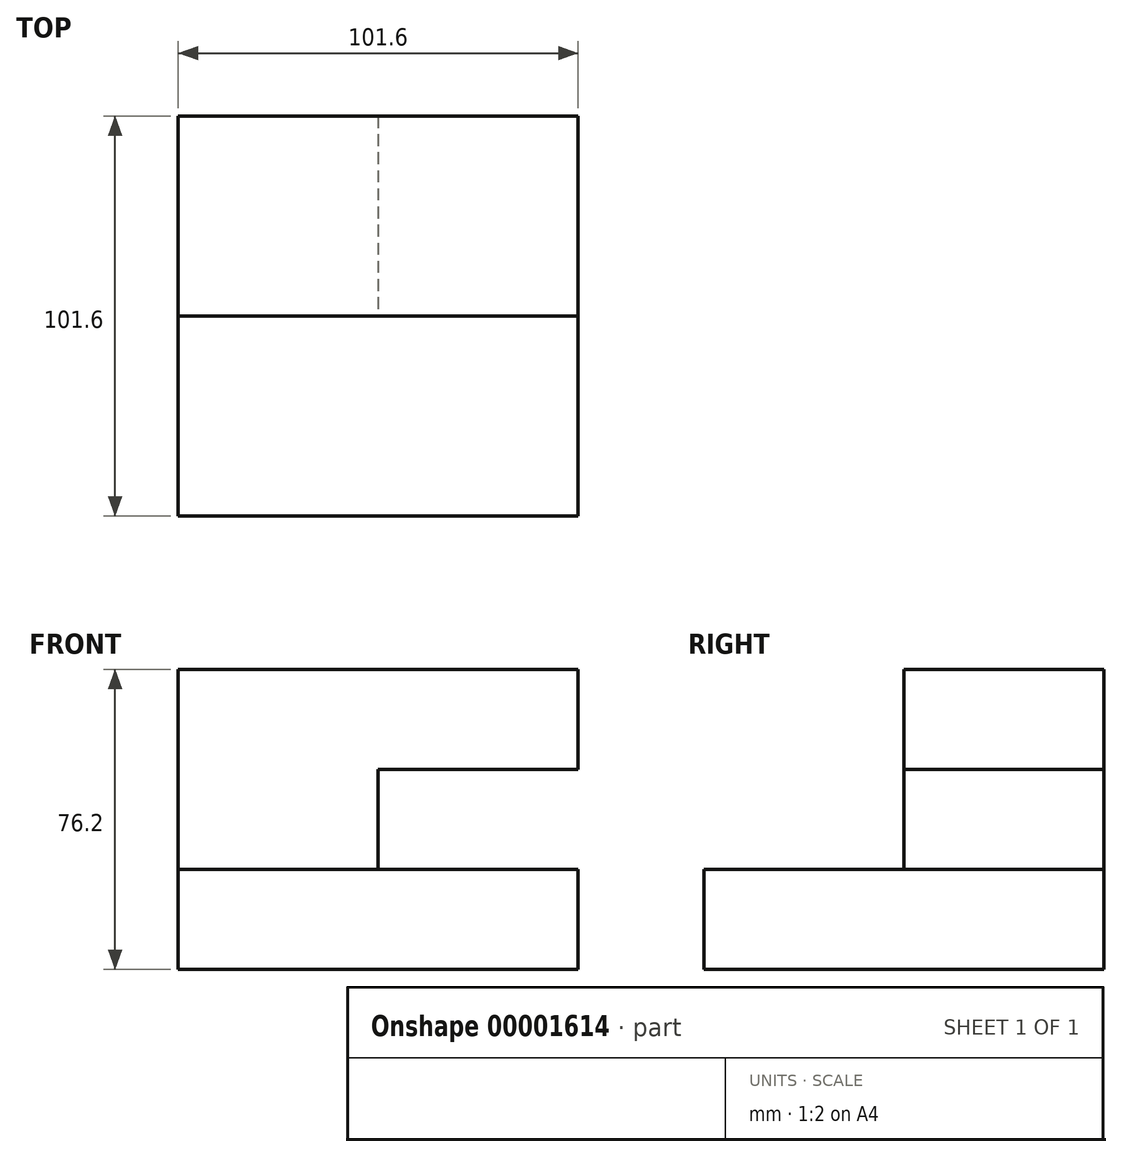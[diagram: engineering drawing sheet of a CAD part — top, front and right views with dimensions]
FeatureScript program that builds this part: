
annotation { "Feature Type Name" : "Feature", "Feature Type Description" : "" }
export const myFeature = defineFeature(function(context is Context, id is Id, definition is map)
    precondition{}
    {
        {
            var Q0;
            Q0=qCreatedBy(makeId("Top.planeOp"),FACE);
            var sketch = newSketch(context, id + "F0", { "sketchPlane" : qUnion([Q0])});
            skLineSegment(sketch, "E0.rect.bottom", {"start": v(50.8, 50.8) * mm, "end": v(-50.8, 50.8) * mm});
            skLineSegment(sketch, "E0.rect.top", {"start": v(50.8, -50.8) * mm, "end": v(-50.8, -50.8) * mm});
            skLineSegment(sketch, "E0.rect.left", {"start": v(50.8, 50.8) * mm, "end": v(50.8, -50.8) * mm});
            skLineSegment(sketch, "E0.rect.right", {"start": v(-50.8, 50.8) * mm, "end": v(-50.8, -50.8) * mm});
            skPoint(sketch, "E0.rect.middle", {"position": v(0, 0) * mm});
            skSolve(sketch);
        }
        {
            var Q0;
            Q0=makeQuery(id+"F0.imprint","IMPRINT",FACE,{"disambiguationData":[TD([[makeQuery(id+"F0.imprint","IMPRINT",EDGE,{"derivedFrom":sQuery(id+"F0.wireOp",EDGE,"E0.rect.bottom")}),1.0]])]});
            extrude(context, id + "F1", {"entities" : qUnion([Q0]), "depth" : 25.4 * mm});
        }
        {
            var Q0;
            Q0=makeQuery(id+"F1.opExtrude","CAP_FACE",FACE,{"disambiguationData":[OSD([sQuery(id+"F0.wireOp",EDGE,"E0.rect.bottom"),sQuery(id+"F0.wireOp",EDGE,"E0.rect.top"),sQuery(id+"F0.wireOp",EDGE,"E0.rect.left"),sQuery(id+"F0.wireOp",EDGE,"E0.rect.right")])],"isStart":false});
            var sketch = newSketch(context, id + "F2", { "sketchPlane" : qUnion([Q0])});
            skLineSegment(sketch, "E1.bottom", {"start": v(-50.8, 50.8) * mm, "end": v(0, 50.8) * mm});
            skLineSegment(sketch, "E1.top", {"start": v(-50.8, 0) * mm, "end": v(0, 0) * mm});
            skLineSegment(sketch, "E1.left", {"start": v(-50.8, 50.8) * mm, "end": v(-50.8, 0) * mm});
            skLineSegment(sketch, "E1.right", {"start": v(0, 50.8) * mm, "end": v(0, 0) * mm});
            skSolve(sketch);
        }
        {
            var Q0;
            Q0=makeQuery(id+"F2.imprint","IMPRINT",FACE,{"disambiguationData":[TD([[makeQuery(id+"F2.imprint","IMPRINT",EDGE,{"derivedFrom":sQuery(id+"F2.wireOp",EDGE,"E1.bottom")}),1.0]])]});
            extrude(context, id + "F3", {"entities" : qUnion([Q0]), "operationType" : NewBodyOperationType.ADD, "depth" : 25.4 * mm});
        }
        {
            var Q0;
            Q0=makeQuery(id+"F3.opExtrude","CAP_FACE",FACE,{"disambiguationData":[OSD([sQuery(id+"F2.wireOp",EDGE,"E1.bottom"),sQuery(id+"F2.wireOp",EDGE,"E1.top"),sQuery(id+"F2.wireOp",EDGE,"E1.left"),sQuery(id+"F2.wireOp",EDGE,"E1.right")])],"isStart":false});
            var sketch = newSketch(context, id + "F4", { "sketchPlane" : qUnion([Q0])});
            skLineSegment(sketch, "E2", {"start": v(0, 0) * mm, "end": v(50.8, 0) * mm});
            skLineSegment(sketch, "E3", {"start": v(50.8, 0) * mm, "end": v(50.8, 50.8) * mm});
            skLineSegment(sketch, "E4", {"start": v(50.8, 50.8) * mm, "end": v(0, 50.8) * mm});
            skSolve(sketch);
        }
        {
            var Q0;
            Q0=qSketchRegion(id+"F4",true);
            var Q1;
            Q1=makeQuery(id+"F4.imprint","IMPRINT",FACE,{"disambiguationData":[TD([[makeQuery(id+"F4.imprint","IMPRINT",EDGE,{"derivedFrom":makeQuery(id+"F3.opExtrude","CAP_EDGE",EDGE,{"disambiguationData":[OSD([sQuery(id+"F2.wireOp",EDGE,"E1.bottom")])],"isStart":false})}),1.0]])]});
            var Q2;
            Q2=makeQuery(id+"F4.imprint","IMPRINT",FACE,{"disambiguationData":[TD([[makeQuery(id+"F4.imprint","IMPRINT",EDGE,{"derivedFrom":sQuery(id+"F4.wireOp",EDGE,"E2")}),1.0]])]});
            extrude(context, id + "F5", {"entities" : qUnion([Q0, Q1, Q2]), "operationType" : NewBodyOperationType.ADD, "depth" : 25.4 * mm});
        }
    });
